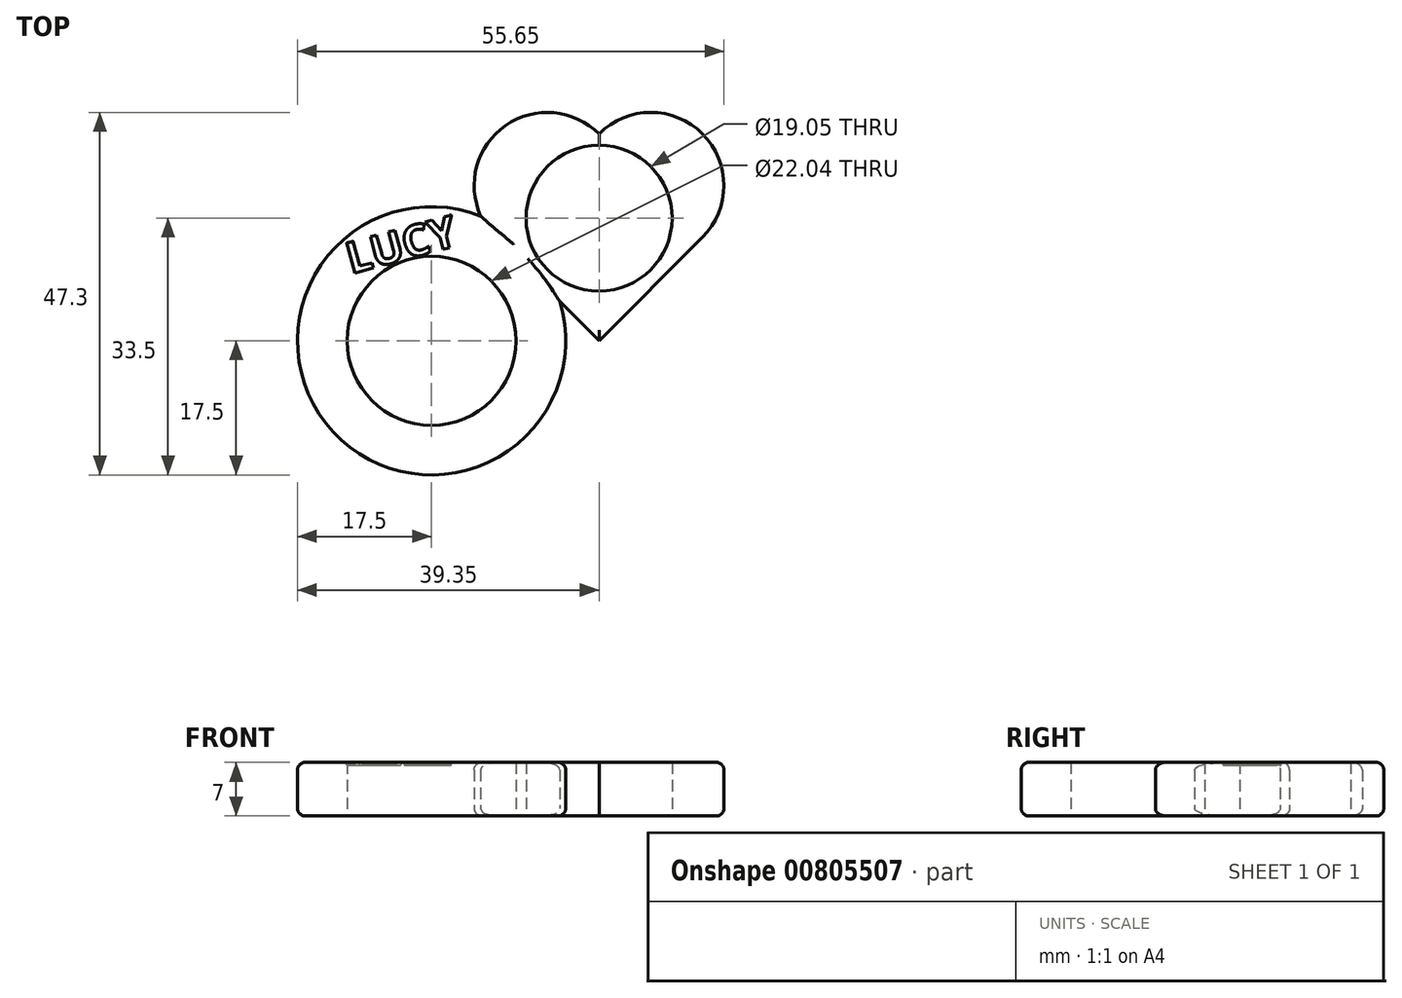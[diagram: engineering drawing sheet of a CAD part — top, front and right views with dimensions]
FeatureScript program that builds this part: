
annotation { "Feature Type Name" : "Feature", "Feature Type Description" : "" }
export const myFeature = defineFeature(function(context is Context, id is Id, definition is map)
    precondition{}
    {
        {
            var Q0;
            Q0=qCreatedBy(makeId("Top.planeOp"),FACE);
            var sketch = newSketch(context, id + "F0", { "sketchPlane" : qUnion([Q0])});
            skLineSegment(sketch, "E0", {"start": v(21.85, 0) * mm, "end": v(21.85, 27) * mm, "construction": true});
            skLineSegment(sketch, "E1", {"start": v(21.85, 0) * mm, "end": v(8.35, 13.5) * mm});
            skArc(sketch, "E2", {"start": v(21.85, 27) * mm, "mid": v(8.35, 27) * mm, "end": v(8.35, 13.5) * mm});
            skArc(sketch, "E3.MirrorCS", {"start": v(21.85, 27) * mm, "mid": v(35.35, 27) * mm, "end": v(35.35, 13.5) * mm});
            skLineSegment(sketch, "E4.MirrorCS", {"start": v(21.85, 0) * mm, "end": v(35.35, 13.5) * mm});
            skCircle(sketch, "E5", {"center": v(21.85, 16) * mm, "radius": 9.53 * mm});
            skSolve(sketch);
        }
        {
            var Q0;
            Q0 = qSketchRegion(id + "F0", true);
            var Q1;
            Q1=makeQuery(id+"F0.imprint","IMPRINT",FACE,{"disambiguationData":[TD([[makeQuery(id+"F0.imprint","IMPRINT",EDGE,{"derivedFrom":sQuery(id+"F0.wireOp",EDGE,"E5")}),-1.0]])]});
            var Q2;
            {var subQ0=sQuery(id+"F0.wireOp",EDGE,"7b1d85c6-0411-4966-a0ee-bd8823eacddd.2");var subQ1=sQuery(id+"F0.wireOp",EDGE,"RbvZz0lY-KInZ-46J4-31RS-xK4GA83J0Fla");var subQ2=makeQuery(id+"F0.imprint","INTERSECT",VERTEX,{"derivedFrom":[subQ1,subQ0]});Q2=makeQuery(id+"F0.imprint","IMPRINT",FACE,{"disambiguationData":[TD([[makeQuery(id+"F0.imprint","IMPRINT",EDGE,{"disambiguationData":[TD([[subQ2,-1.0]])],"derivedFrom":subQ1}),-1.0]])]});}
            extrude(context, id + "F1", {"entities" : qUnion([Q0, Q1, Q2]), "depth" : 7 * mm, "offsetDistance" : 25 * mm});
        }
        {
            var Q0;
            Q0=qCreatedBy(makeId("Right.planeOp"),FACE);
            var sketch = newSketch(context, id + "F2", { "sketchPlane" : qUnion([Q0])});
            skLineSegment(sketch, "E6", {"start": v(0, 0) * mm, "end": v(0, 36.39) * mm, "construction": true});
            skSolve(sketch);
        }
        {
            var Q0;
            Q0=makeQuery(id+"F1.opExtrude","CAP_FACE",FACE,{"disambiguationData":[OSD([sQuery(id+"F0.wireOp",EDGE,"E1"),sQuery(id+"F0.wireOp",EDGE,"E2"),sQuery(id+"F0.wireOp",EDGE,"E3.MirrorCS"),sQuery(id+"F0.wireOp",EDGE,"E4.MirrorCS"),sQuery(id+"F0.wireOp",EDGE,"RbvZz0lY-KInZ-46J4-31RS-xK4GA83J0Fla"),sQuery(id+"F0.wireOp",EDGE,"IvNz5zkU-zYmy-Vkzp-Leyy-1xtyaDibWg19"),sQuery(id+"F0.wireOp",EDGE,"E5")])],"isStart":false});
            var sketch = newSketch(context, id + "F3", { "sketchPlane" : qUnion([Q0])});
            skArc(sketch, "E7.0", {"start": v(21.85, 27) * mm, "mid": v(8.35, 27) * mm, "end": v(8.35, 13.5) * mm});
            skArc(sketch, "E8.0", {"start": v(21.85, 27) * mm, "mid": v(35.35, 27) * mm, "end": v(35.35, 13.5) * mm});
            skLineSegment(sketch, "E9.0", {"start": v(21.85, 0) * mm, "end": v(8.35, 13.5) * mm});
            skPoint(sketch, "E10.0", {"position": v(28.6, 6.75) * mm});
            skLineSegment(sketch, "E11.0", {"start": v(21.85, 0) * mm, "end": v(35.35, 13.5) * mm});
            skSolve(sketch);
        }
        {
            var Q0;
            Q0=makeQuery(id+"F1.opExtrude","CAP_EDGE",EDGE,{"disambiguationData":[OSD([sQuery(id+"F0.wireOp",EDGE,"E2")])],"isStart":false});
            var Q1;
            Q1=makeQuery(id+"F1.opExtrude","CAP_EDGE",EDGE,{"disambiguationData":[OSD([sQuery(id+"F0.wireOp",EDGE,"E3.MirrorCS")])],"isStart":false});
            var Q2;
            Q2=makeQuery(id+"F1.opExtrude","CAP_EDGE",EDGE,{"disambiguationData":[OSD([sQuery(id+"F0.wireOp",EDGE,"E4.MirrorCS")])],"isStart":true});
            var Q3;
            Q3=makeQuery(id+"F1.opExtrude","CAP_EDGE",EDGE,{"disambiguationData":[OSD([sQuery(id+"F0.wireOp",EDGE,"E4.MirrorCS")])],"isStart":false});
            var Q4;
            Q4=makeQuery(id+"F1.opExtrude","CAP_EDGE",EDGE,{"disambiguationData":[OSD([sQuery(id+"F0.wireOp",EDGE,"E1")])],"isStart":false});
            var Q5;
            Q5=makeQuery(id+"F1.opExtrude","CAP_EDGE",EDGE,{"disambiguationData":[OSD([sQuery(id+"F0.wireOp",EDGE,"E1")])],"isStart":true});
            var Q6;
            Q6=makeQuery(id+"F1.opExtrude","CAP_EDGE",EDGE,{"disambiguationData":[OSD([sQuery(id+"F0.wireOp",EDGE,"E2")])],"isStart":true});
            var Q7;
            Q7=makeQuery(id+"F1.opExtrude","CAP_EDGE",EDGE,{"disambiguationData":[OSD([sQuery(id+"F0.wireOp",EDGE,"E3.MirrorCS")])],"isStart":true});
            fillet(context, id + "F4", {"entities" : qUnion([Q0, Q1, Q2, Q3, Q4, Q5, Q6, Q7]), "radius" : 1 * mm, "tangentPropagation" : true, "allowEdgeOverflow" : false});
        }
        {
            var Q0;
            Q0=qCreatedBy(makeId("Top.planeOp"),FACE);
            var sketch = newSketch(context, id + "F5", { "sketchPlane" : qUnion([Q0])});
            skCircle(sketch, "E12", {"center": v(0, 0) * mm, "radius": 17.5 * mm});
            skCircle(sketch, "E13", {"center": v(0, 0) * mm, "radius": 11.02 * mm});
            skSolve(sketch);
        }
        {
            var Q0;
            Q0=makeQuery(id+"F5.imprint","IMPRINT",FACE,{"disambiguationData":[TD([[makeQuery(id+"F5.imprint","IMPRINT",EDGE,{"derivedFrom":sQuery(id+"F5.wireOp",EDGE,"E12")}),1.0]])]});
            extrude(context, id + "F6", {"entities" : qUnion([Q0]), "depth" : 7 * mm, "offsetDistance" : 25 * mm});
        }
        {
            var Q0;
            Q0=makeQuery(id+"F6.opExtrude","CAP_EDGE",EDGE,{"disambiguationData":[OSD([sQuery(id+"F5.wireOp",EDGE,"E12")])],"isStart":false});
            var Q1;
            Q1=makeQuery(id+"F6.opExtrude","CAP_EDGE",EDGE,{"disambiguationData":[OSD([sQuery(id+"F5.wireOp",EDGE,"E12")])],"isStart":true});
            fillet(context, id + "F7", {"entities" : qUnion([Q0, Q1]), "radius" : 1 * mm, "tangentPropagation" : true, "allowEdgeOverflow" : false});
        }
        {
            var Q0;
            Q0=makeQuery(id+"F1.opExtrude","SWEPT_BODY",BODY,{"disambiguationData":[OSD([sQuery(id+"F0.wireOp",EDGE,"E1"),sQuery(id+"F0.wireOp",EDGE,"E2"),sQuery(id+"F0.wireOp",EDGE,"E3.MirrorCS"),sQuery(id+"F0.wireOp",EDGE,"E4.MirrorCS"),sQuery(id+"F0.wireOp",EDGE,"E5")])]});
            var Q1;
            Q1=makeQuery(id+"FtXFM8Vc4bFr5bj_1.1.F1.opExtrude","SWEPT_BODY",BODY,{"disambiguationData":[OSD([sQuery(id+"F0.wireOp",EDGE,"E1"),sQuery(id+"F0.wireOp",EDGE,"E2"),sQuery(id+"F0.wireOp",EDGE,"E3.MirrorCS"),sQuery(id+"F0.wireOp",EDGE,"E4.MirrorCS"),sQuery(id+"F0.wireOp",EDGE,"E5")])]});
            var Q2;
            Q2=makeQuery(id+"FtXFM8Vc4bFr5bj_1.2.F1.opExtrude","SWEPT_BODY",BODY,{"disambiguationData":[OSD([sQuery(id+"F0.wireOp",EDGE,"E1"),sQuery(id+"F0.wireOp",EDGE,"E2"),sQuery(id+"F0.wireOp",EDGE,"E3.MirrorCS"),sQuery(id+"F0.wireOp",EDGE,"E4.MirrorCS"),sQuery(id+"F0.wireOp",EDGE,"E5")])]});
            var Q3;
            Q3=makeQuery(id+"F6.opExtrude","SWEPT_BODY",BODY,{"disambiguationData":[OSD([sQuery(id+"F5.wireOp",EDGE,"E12"),sQuery(id+"F5.wireOp",EDGE,"E13")])]});
            booleanBodies(context, id + "F8", {"operationType" : BooleanOperationType.UNION, "tools" : qUnion([Q0, Q1, Q2, Q3])});
        }
        {
            var Q0;
            {var subQ0=sQuery(id+"F0.wireOp",EDGE,"E5");var subQ1=sQuery(id+"F0.wireOp",EDGE,"E4.MirrorCS");var subQ2=sQuery(id+"F0.wireOp",EDGE,"E3.MirrorCS");var subQ3=sQuery(id+"F0.wireOp",EDGE,"E2");var subQ4=sQuery(id+"F0.wireOp",EDGE,"E1");Q0=makeQuery(id+"F8.opBoolean","MERGE",FACE,{"derivedFrom":[makeQuery(id+"F1.opExtrude","CAP_FACE",FACE,{"disambiguationData":[OSD([subQ4,subQ3,subQ2,subQ1,subQ0])],"isStart":false}),makeQuery(id+"FtXFM8Vc4bFr5bj_1.1.F1.opExtrude","CAP_FACE",FACE,{"disambiguationData":[OSD([subQ4,subQ3,subQ2,subQ1,subQ0])],"isStart":false}),makeQuery(id+"FtXFM8Vc4bFr5bj_1.2.F1.opExtrude","CAP_FACE",FACE,{"disambiguationData":[OSD([subQ4,subQ3,subQ2,subQ1,subQ0])],"isStart":false}),makeQuery(id+"F6.opExtrude","CAP_FACE",FACE,{"disambiguationData":[OSD([sQuery(id+"F5.wireOp",EDGE,"E12"),sQuery(id+"F5.wireOp",EDGE,"E13")])],"isStart":false})]});}
            var sketch = newSketch(context, id + "F9", { "sketchPlane" : qUnion([Q0])});
            skText(sketch, "E14", { "text": "LUCY", "fontName": "OpenSans-Bold.ttf"});
            skLineSegment(sketch, "E15", {"start": v(-15.56, 5.5) * mm, "end": v(10.73, 12.54) * mm, "construction": true});
            const initialGuessF9  = {"E14": [-0.01051, 0.00872, 0.96593, 0.25882, 0.00408]};
            skSetInitialGuess(sketch, initialGuessF9);
            skSolve(sketch);
        }
        {
            var Q0;
            Q0 = qSketchRegion(id + "F9", true);
            extrude(context, id + "F10", {"entities" : qUnion([Q0]), "operationType" : NewBodyOperationType.REMOVE, "oppositeDirection" : true, "depth" : .4 * mm, "offsetDistance" : 25 * mm});
        }
    });
